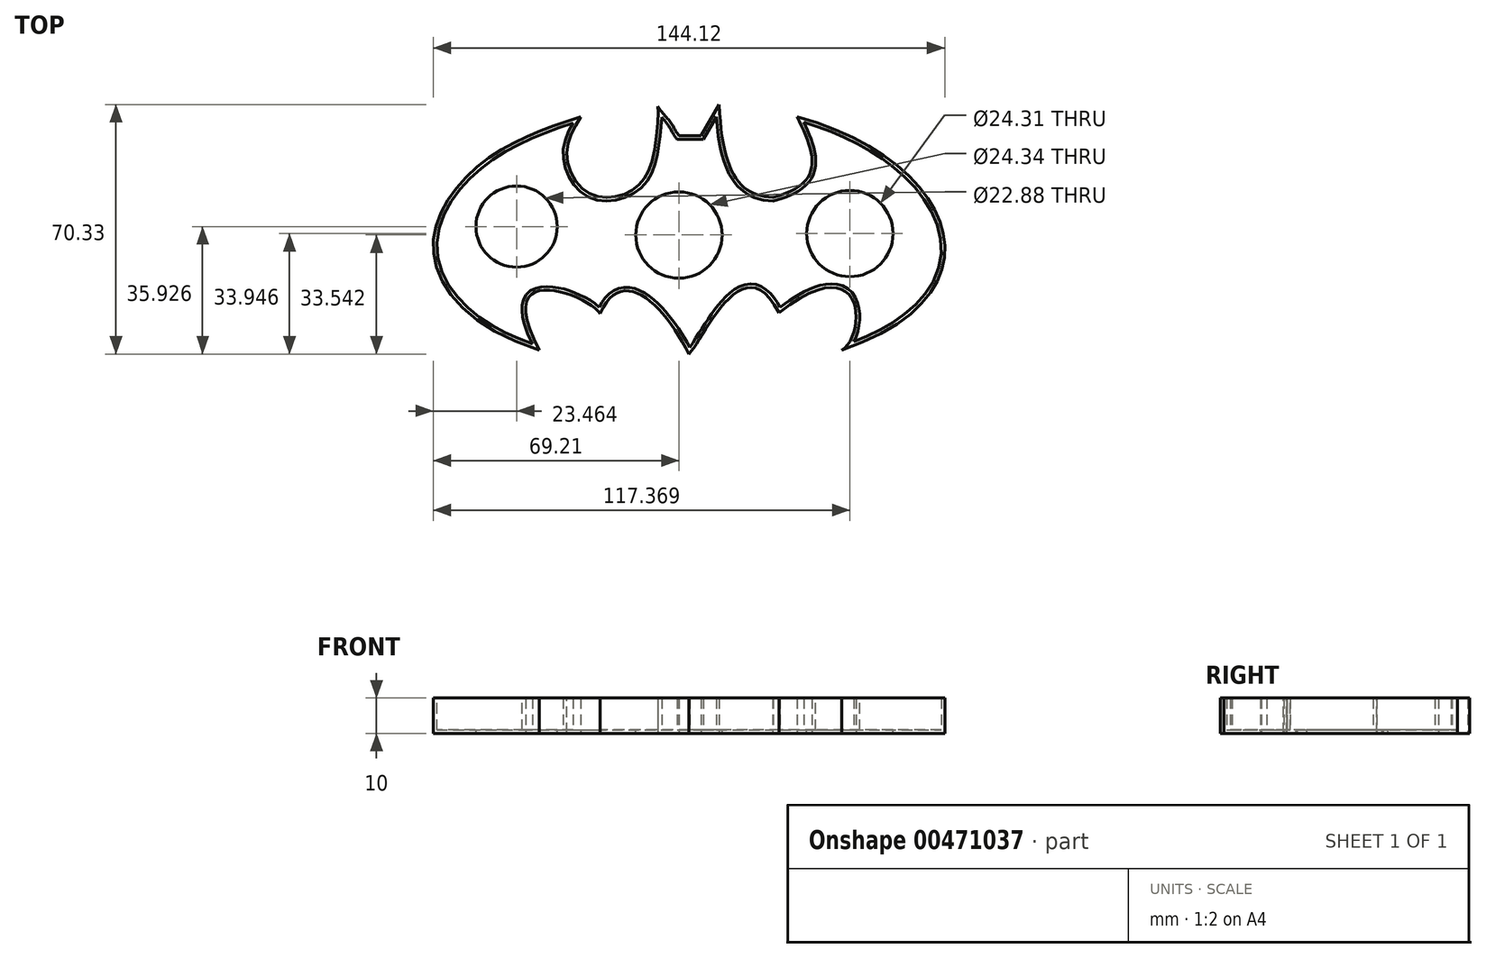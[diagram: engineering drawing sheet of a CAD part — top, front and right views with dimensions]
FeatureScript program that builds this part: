
annotation { "Feature Type Name" : "Feature", "Feature Type Description" : "" }
export const myFeature = defineFeature(function(context is Context, id is Id, definition is map)
    precondition{}
    {
        {
            var Q0;
            Q0=qCreatedBy(makeId("Top.planeOp"),FACE);
            var sketch = newSketch(context, id + "F0", { "sketchPlane" : qUnion([Q0])});
            skFitSpline(sketch, "E0", {"points": [v(-27.64, 35.88) * mm, v(-54.4, 23.63) * mm, v(-69.2, 0) * mm, v(-39.31, -29.9) * mm], "startDerivative": vector(-86.96, -28.73) * mm, "endDerivative": vector(165.03, -52) * mm});
            skFitSpline(sketch, "E1", {"points": [v(-27.64, 35.88) * mm, v(-31.62, 25.91) * mm, v(-27.64, 15.95) * mm, v(-19.38, 13.1) * mm, v(-11.4, 16.51) * mm, v(-7.14, 25.34) * mm, v(-6, 38.72) * mm, v(-6.28, 38.72) * mm], "startDerivative": vector(-34.75, -57.82) * mm, "endDerivative": vector(-11.48, -5.45) * mm});
            skFitSpline(sketch, "E2", {"points": [v(-6, 38.72) * mm, v(-2.3, 34.17) * mm, v(0, 30.47) * mm], "startDerivative": vector(5.2, -7.7) * mm, "endDerivative": vector(6.76, -8.8) * mm});
            skLineSegment(sketch, "E3", {"start": v(0, 30.47) * mm, "end": v(6.25, 30.47) * mm});
            skFitSpline(sketch, "E4", {"points": [v(6.25, 30.47) * mm, v(11.37, 39.3) * mm], "startDerivative": vector(10.25, 17.65) * mm, "endDerivative": vector(5.13, 8.83) * mm});
            skFitSpline(sketch, "E5", {"points": [v(11.37, 39.3) * mm, v(26.46, 13.1) * mm], "startDerivative": vector(1.7, -58.09) * mm, "endDerivative": vector(27.33, -0.85) * mm});
            skFitSpline(sketch, "E6", {"points": [v(33.3, 35.88) * mm, v(26.46, 13.1) * mm], "startDerivative": vector(15.38, -31.6) * mm, "endDerivative": vector(-45.27, -11.96) * mm});
            skFitSpline(sketch, "E7", {"points": [v(33.3, 35.88) * mm, v(45.82, -29.9) * mm], "startDerivative": vector(131.55, -35.88) * mm, "endDerivative": vector(-144.36, -48.69) * mm});
            skFitSpline(sketch, "E8", {"points": [v(28.17, -19.36) * mm, v(45.82, -29.9) * mm], "startDerivative": vector(74.32, 58.09) * mm, "endDerivative": vector(-21.35, -11.96) * mm});
            skFitSpline(sketch, "E9", {"points": [v(28.17, -19.36) * mm, v(2.83, -31.04) * mm], "startDerivative": vector(-29.9, 58.09) * mm, "endDerivative": vector(-13.67, -15.38) * mm});
            skFitSpline(sketch, "E10", {"points": [v(2.83, -31.04) * mm, v(-22.23, -19.65) * mm], "startDerivative": vector(-20.5, 41) * mm, "endDerivative": vector(-18.8, -42.7) * mm});
            skFitSpline(sketch, "E11", {"points": [v(-39.31, -29.9) * mm, v(-22.23, -19.65) * mm], "startDerivative": vector(-41.86, 77.73) * mm, "endDerivative": vector(10.25, -16.23) * mm});
            skCircle(sketch, "E12", {"center": v(-45.75, 4.89) * mm, "radius": 10.44 * mm});
            skCircle(sketch, "E13", {"center": v(0, 2.5) * mm, "radius": 11.17 * mm});
            skCircle(sketch, "E14", {"center": v(48.16, 2.9) * mm, "radius": 11.15 * mm});
            skSolve(sketch);
        }
        {
            var Q0;
            {var subQ0=sQuery(id+"F0.wireOp",EDGE,"E0");Q0=makeQuery(id+"F0.imprint","IMPRINT",FACE,{"disambiguationData":[TD([[makeQuery(id+"F0.imprint","IMPRINT",EDGE,{"derivedFrom":subQ0}),1.0]])]});}
            extrude(context, id + "F1", {"entities" : qUnion([Q0]), "depth" : 10 * mm});
        }
        {
            var Q0;
            Q0=makeQuery(id+"F1.opExtrude","CAP_FACE",FACE,{"disambiguationData":[OSD([sQuery(id+"F0.wireOp",EDGE,"E0"),sQuery(id+"F0.wireOp",EDGE,"E1"),sQuery(id+"F0.wireOp",EDGE,"E2"),sQuery(id+"F0.wireOp",EDGE,"E3"),sQuery(id+"F0.wireOp",EDGE,"E4"),sQuery(id+"F0.wireOp",EDGE,"E5"),sQuery(id+"F0.wireOp",EDGE,"E6"),sQuery(id+"F0.wireOp",EDGE,"E7"),sQuery(id+"F0.wireOp",EDGE,"E8"),sQuery(id+"F0.wireOp",EDGE,"E9"),sQuery(id+"F0.wireOp",EDGE,"E10"),sQuery(id+"F0.wireOp",EDGE,"E11")])],"isStart":false});
            shell(context, id + "F2", {"entities" : qUnion([Q0]), "thickness" : 1 * mm});
        }
        {
            var Q0;
            Q0=makeQuery(id+"F0.imprint","IMPRINT",FACE,{"disambiguationData":[TD([[makeQuery(id+"F0.imprint","IMPRINT",EDGE,{"derivedFrom":sQuery(id+"F0.wireOp",EDGE,"E12")}),1.0]])]});
            extrude(context, id + "F3", {"entities" : qUnion([Q0]), "operationType" : NewBodyOperationType.REMOVE, "oppositeDirection" : true, "depth" : 25 * mm});
        }
        {
            var Q0;
            {var subQ0=sQuery(id+"F0.wireOp",EDGE,"E12");var subQ1=sQuery(id+"F0.wireOp",EDGE,"E11");var subQ2=sQuery(id+"F0.wireOp",EDGE,"E10");var subQ3=sQuery(id+"F0.wireOp",EDGE,"E9");var subQ4=sQuery(id+"F0.wireOp",EDGE,"E8");var subQ5=sQuery(id+"F0.wireOp",EDGE,"E7");var subQ6=sQuery(id+"F0.wireOp",EDGE,"E6");var subQ7=sQuery(id+"F0.wireOp",EDGE,"E5");var subQ8=sQuery(id+"F0.wireOp",EDGE,"E4");var subQ9=sQuery(id+"F0.wireOp",EDGE,"E3");var subQ10=sQuery(id+"F0.wireOp",EDGE,"E2");var subQ11=sQuery(id+"F0.wireOp",EDGE,"E1");var subQ12=sQuery(id+"F0.wireOp",EDGE,"E0");Q0=makeQuery(id+"F2.opShell","OFFSET_FACE",FACE,{"disambiguationData":[OSD([subQ12,subQ11,subQ10,subQ9,subQ8,subQ7,subQ6,subQ5,subQ4,subQ3,subQ2,subQ1,subQ0]),TDD([makeQuery(id+"F1.opExtrude","CAP_FACE",FACE,{"disambiguationData":[OSD([subQ12,subQ11,subQ10,subQ9,subQ8,subQ7,subQ6,subQ5,subQ4,subQ3,subQ2,subQ1,subQ0])],"isStart":false})])]});}
            extrude(context, id + "F4", {"entities" : qUnion([Q0]), "operationType" : NewBodyOperationType.REMOVE, "oppositeDirection" : true, "depth" : 25 * mm});
        }
    });
